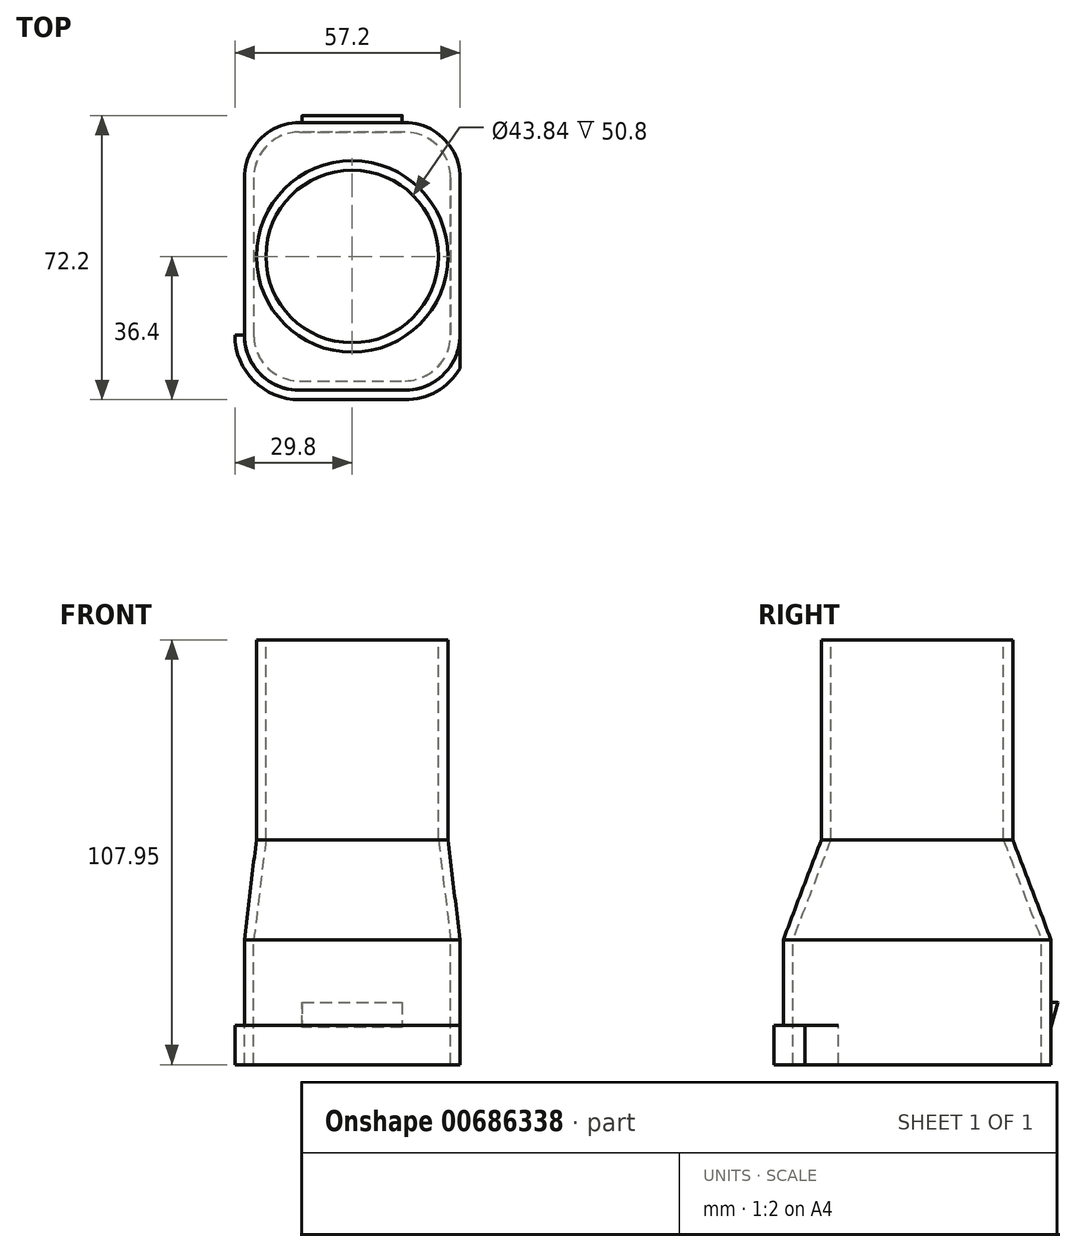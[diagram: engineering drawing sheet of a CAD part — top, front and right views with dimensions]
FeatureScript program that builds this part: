
annotation { "Feature Type Name" : "Feature", "Feature Type Description" : "" }
export const myFeature = defineFeature(function(context is Context, id is Id, definition is map)
    precondition{}
    {
        {
            var Q0;
            Q0=qCreatedBy(makeId("Top.planeOp"),FACE);
            var sketch = newSketch(context, id + "F0", { "sketchPlane" : qUnion([Q0])});
            skLineSegment(sketch, "E0.bottom", {"start": v(-13.4, 34) * mm, "end": v(13.4, 34) * mm});
            skLineSegment(sketch, "E0.top", {"start": v(-13.4, -34) * mm, "end": v(13.4, -34) * mm});
            skLineSegment(sketch, "E0.left", {"start": v(-27.4, 20) * mm, "end": v(-27.4, -20) * mm});
            skLineSegment(sketch, "E0.right", {"start": v(27.4, 20) * mm, "end": v(27.4, -20) * mm});
            skLineSegment(sketch, "E1", {"start": v(0, 0) * mm, "end": v(0, 34) * mm});
            skPoint(sketch, "E2.visualSharp", {"position": v(27.4, 34) * mm});
            skArc(sketch, "E2.filletArc", {"start": v(27.4, 20) * mm, "mid": v(23.3, 29.9) * mm, "end": v(13.4, 34) * mm});
            skPoint(sketch, "E3.visualSharp", {"position": v(27.4, -34) * mm});
            skArc(sketch, "E3.filletArc", {"start": v(13.4, -34) * mm, "mid": v(23.3, -29.9) * mm, "end": v(27.4, -20) * mm});
            skPoint(sketch, "E4.visualSharp", {"position": v(-27.4, -34) * mm});
            skArc(sketch, "E4.filletArc", {"start": v(-27.4, -20) * mm, "mid": v(-23.3, -29.9) * mm, "end": v(-13.4, -34) * mm});
            skPoint(sketch, "E5.visualSharp", {"position": v(-27.4, 34) * mm});
            skArc(sketch, "E5.filletArc", {"start": v(-13.4, 34) * mm, "mid": v(-23.3, 29.9) * mm, "end": v(-27.4, 20) * mm});
            skArc(sketch, "E6.0", {"start": v(-13.4, 31.6) * mm, "mid": v(-21.6, 28.2) * mm, "end": v(-25, 20) * mm});
            skLineSegment(sketch, "E6.1", {"start": v(-13.4, 31.6) * mm, "end": v(13.4, 31.6) * mm});
            skLineSegment(sketch, "E6.2", {"start": v(-25, 20) * mm, "end": v(-25, -20) * mm});
            skArc(sketch, "E6.3", {"start": v(25, 20) * mm, "mid": v(21.6, 28.2) * mm, "end": v(13.4, 31.6) * mm});
            skArc(sketch, "E6.4", {"start": v(-25, -20) * mm, "mid": v(-21.6, -28.2) * mm, "end": v(-13.4, -31.6) * mm});
            skLineSegment(sketch, "E6.5", {"start": v(-13.4, -31.6) * mm, "end": v(13.4, -31.6) * mm});
            skArc(sketch, "E6.6", {"start": v(13.4, -31.6) * mm, "mid": v(21.6, -28.2) * mm, "end": v(25, -20) * mm});
            skLineSegment(sketch, "E6.7", {"start": v(25, 20) * mm, "end": v(25, -20) * mm});
            skSolve(sketch);
        }
        {
            var Q0;
            Q0 = qSketchRegion(id + "F0", true);
            var Q1;
            {var subQ3=sQuery(id+"F0.wireOp",EDGE,"E6.0");Q1=makeQuery(id+"F0.imprint","IMPRINT",FACE,{"disambiguationData":[TD([[makeQuery(id+"F0.imprint","IMPRINT",EDGE,{"derivedFrom":subQ3}),1.0]])]});}
            extrude(context, id + "F1", {"entities" : qUnion([Q0, Q1]), "oppositeDirection" : true, "depth" : 31.75 * mm, "offsetDistance" : 25.4 * mm});
        }
        {
            var Q0;
            Q0=makeQuery(id+"F1.opExtrude","SWEPT_FACE",FACE,{"disambiguationData":[OSD([sQuery(id+"F0.wireOp",EDGE,"E0.bottom")])]});
            var sketch = newSketch(context, id + "F2", { "sketchPlane" : qUnion([Q0])});
            skLineSegment(sketch, "E7", {"start": v(0, 0) * mm, "end": v(0, -15.88) * mm});
            skLineSegment(sketch, "E8", {"start": v(0, -15.88) * mm, "end": v(-12.7, -15.88) * mm});
            skLineSegment(sketch, "E9.bottom", {"start": v(-12.7, -15.88) * mm, "end": v(12.7, -15.88) * mm});
            skLineSegment(sketch, "E9.top", {"start": v(-12.7, -22.22) * mm, "end": v(12.7, -22.22) * mm});
            skLineSegment(sketch, "E9.left", {"start": v(-12.7, -15.88) * mm, "end": v(-12.7, -22.22) * mm});
            skLineSegment(sketch, "E9.right", {"start": v(12.7, -15.88) * mm, "end": v(12.7, -22.22) * mm});
            skSolve(sketch);
        }
        {
            var Q0;
            Q0 = qSketchRegion(id + "F2", true);
            extrude(context, id + "F3", {"entities" : qUnion([Q0]), "operationType" : NewBodyOperationType.ADD, "depth" : 1.8 * mm, "offsetDistance" : 25.4 * mm});
        }
        {
            var Q0;
            Q0=makeQuery(id+"F3.opExtrude","SWEPT_FACE",FACE,{"disambiguationData":[OSD([sQuery(id+"F2.wireOp",EDGE,"E9.left")])]});
            var sketch = newSketch(context, id + "F4", { "sketchPlane" : qUnion([Q0])});
            skCircle(sketch, "E10", {"center": v(35.75, -15.93) * mm, "radius": 0.05 * mm});
            skLineSegment(sketch, "E11", {"start": v(35.78, -15.97) * mm, "end": v(34, -22.22) * mm});
            skLineSegment(sketch, "E12", {"start": v(34, -22.22) * mm, "end": v(35.8, -22.22) * mm});
            skLineSegment(sketch, "E13", {"start": v(35.8, -22.22) * mm, "end": v(35.8, -15.93) * mm});
            skLineSegment(sketch, "E14", {"start": v(35.8, -15.93) * mm, "end": v(35.8, -15.88) * mm});
            skLineSegment(sketch, "E15", {"start": v(35.8, -15.88) * mm, "end": v(35.75, -15.88) * mm});
            skSolve(sketch);
        }
        {
            var Q0;
            {var subQ0=sQuery(id+"F4.wireOp",EDGE,"E14");Q0=makeQuery(id+"F4.imprint","IMPRINT",FACE,{"disambiguationData":[TD([[makeQuery(id+"F4.imprint","IMPRINT",EDGE,{"derivedFrom":subQ0}),-1.0]])]});}
            var Q1;
            {var subQ0=sQuery(id+"F4.wireOp",EDGE,"E11");Q1=makeQuery(id+"F4.imprint","IMPRINT",FACE,{"disambiguationData":[TD([[makeQuery(id+"F4.imprint","IMPRINT",EDGE,{"derivedFrom":subQ0}),1.0]])]});}
            extrude(context, id + "F5", {"entities" : qUnion([Q0, Q1]), "operationType" : NewBodyOperationType.REMOVE, "endBound" : BoundingType.THROUGH_ALL, "oppositeDirection" : true, "depth" : 25.4 * mm, "offsetDistance" : 25.4 * mm});
        }
        {
            var Q0;
            Q0=qCreatedBy(makeId("Top.planeOp"),FACE);
            cPlane(context, id + "F6", {"entities" : qUnion([Q0]), "cplaneType" : CPlaneType.OFFSET, "offset" : 76.2 * mm, "width" : 152.4 * mm, "height" : 152.4 * mm});
        }
        {
            var Q0;
            Q0=qCreatedBy(id+"F6.planeOp",FACE);
            var sketch = newSketch(context, id + "F7", { "sketchPlane" : qUnion([Q0])});
            skCircle(sketch, "E16", {"center": v(0, 0) * mm, "radius": 24.32 * mm});
            skCircle(sketch, "E17", {"center": v(0, 0) * mm, "radius": 21.92 * mm});
            skSolve(sketch);
        }
        {
            var Q0;
            Q0 = qSketchRegion(id + "F7", true);
            var Q1;
            Q1=makeQuery(id+"F7.imprint","IMPRINT",FACE,{"disambiguationData":[TD([[makeQuery(id+"F7.imprint","IMPRINT",EDGE,{"derivedFrom":sQuery(id+"F7.wireOp",EDGE,"E17")}),1.0]])]});
            extrude(context, id + "F8", {"entities" : qUnion([Q0, Q1]), "oppositeDirection" : true, "depth" : 50.8 * mm, "offsetDistance" : 25.4 * mm});
        }
        {
            var Q1;
            Q1=makeQuery(id+"F1.opExtrude","CAP_FACE",FACE,{"disambiguationData":[OSD([sQuery(id+"F0.wireOp",EDGE,"E0.bottom"),sQuery(id+"F0.wireOp",EDGE,"E0.top"),sQuery(id+"F0.wireOp",EDGE,"E0.left"),sQuery(id+"F0.wireOp",EDGE,"E0.right"),sQuery(id+"F0.wireOp",EDGE,"E2.filletArc"),sQuery(id+"F0.wireOp",EDGE,"E3.filletArc"),sQuery(id+"F0.wireOp",EDGE,"E4.filletArc"),sQuery(id+"F0.wireOp",EDGE,"E5.filletArc")])],"isStart":true});
            var Q2;
            Q2=makeQuery(id+"F8.opExtrude","CAP_FACE",FACE,{"disambiguationData":[OSD([sQuery(id+"F7.wireOp",EDGE,"E16")])],"isStart":false});
            loft(context, id + "F9", {"operationType" : NewBodyOperationType.ADD, "sheetProfilesArray" : [{ "sheetProfileEntities" : qUnion([Q1]) }, { "sheetProfileEntities" : qUnion([Q2]) }]});
        }
        {
            var Q0;
            Q0=makeQuery(id+"F7.imprint","IMPRINT",FACE,{"disambiguationData":[TD([[makeQuery(id+"F7.imprint","IMPRINT",EDGE,{"derivedFrom":sQuery(id+"F7.wireOp",EDGE,"E17")}),1.0]])]});
            extrude(context, id + "F10", {"entities" : qUnion([Q0]), "operationType" : NewBodyOperationType.REMOVE, "oppositeDirection" : true, "depth" : 50.8 * mm, "offsetDistance" : 25.4 * mm});
        }
        {
            var Q0;
            {var subQ3=sQuery(id+"F0.wireOp",EDGE,"E6.0");Q0=makeQuery(id+"F0.imprint","IMPRINT",FACE,{"disambiguationData":[TD([[makeQuery(id+"F0.imprint","IMPRINT",EDGE,{"derivedFrom":subQ3}),1.0]])]});}
            extrude(context, id + "F11", {"entities" : qUnion([Q0]), "operationType" : NewBodyOperationType.REMOVE, "oppositeDirection" : true, "depth" : 50.8 * mm, "offsetDistance" : 25.4 * mm});
        }
        {
            var Q1;
            Q1=makeQuery(id+"F11.boolean.opBoolean","COPY",FACE,{"derivedFrom":makeQuery(id+"F11.opExtrude","CAP_FACE",FACE,{"disambiguationData":[OSD([sQuery(id+"F0.wireOp",EDGE,"E6.0"),sQuery(id+"F0.wireOp",EDGE,"E6.1"),sQuery(id+"F0.wireOp",EDGE,"E6.2"),sQuery(id+"F0.wireOp",EDGE,"E6.3"),sQuery(id+"F0.wireOp",EDGE,"E6.4"),sQuery(id+"F0.wireOp",EDGE,"E6.5"),sQuery(id+"F0.wireOp",EDGE,"E6.6"),sQuery(id+"F0.wireOp",EDGE,"E6.7")])],"isStart":true})});
            var Q2;
            Q2=makeQuery(id+"F10.boolean.opBoolean","COPY",FACE,{"derivedFrom":makeQuery(id+"F10.opExtrude","CAP_FACE",FACE,{"disambiguationData":[OSD([sQuery(id+"F7.wireOp",EDGE,"E17")])],"isStart":false})});
            loft(context, id + "F12", {"operationType" : NewBodyOperationType.REMOVE, "sheetProfilesArray" : [{ "sheetProfileEntities" : qUnion([Q1]) }, { "sheetProfileEntities" : qUnion([Q2]) }]});
        }
        {
            var Q0;
            Q0=makeQuery(id+"F1.opExtrude","CAP_FACE",FACE,{"disambiguationData":[OSD([sQuery(id+"F0.wireOp",EDGE,"E0.bottom"),sQuery(id+"F0.wireOp",EDGE,"E0.top"),sQuery(id+"F0.wireOp",EDGE,"E0.left"),sQuery(id+"F0.wireOp",EDGE,"E0.right"),sQuery(id+"F0.wireOp",EDGE,"E2.filletArc"),sQuery(id+"F0.wireOp",EDGE,"E3.filletArc"),sQuery(id+"F0.wireOp",EDGE,"E4.filletArc"),sQuery(id+"F0.wireOp",EDGE,"E5.filletArc")])],"isStart":false});
            var sketch = newSketch(context, id + "F13", { "sketchPlane" : qUnion([Q0])});
            skLineSegment(sketch, "E18", {"start": v(27.4, 20) * mm, "end": v(27.4, 28.54) * mm});
            skArc(sketch, "E19.0", {"start": v(13.4, 36.4) * mm, "mid": v(21.43, 34.3) * mm, "end": v(27.4, 28.54) * mm});
            skLineSegment(sketch, "E19.1", {"start": v(-13.4, 36.4) * mm, "end": v(13.4, 36.4) * mm});
            skArc(sketch, "E19.2", {"start": v(-29.8, 20) * mm, "mid": v(-25, 31.6) * mm, "end": v(-13.4, 36.4) * mm});
            skLineSegment(sketch, "E20", {"start": v(-29.8, 20) * mm, "end": v(-25, 20) * mm});
            skArc(sketch, "E21.0", {"start": v(13.4, 32) * mm, "mid": v(21.89, 28.49) * mm, "end": v(25.4, 20) * mm});
            skLineSegment(sketch, "E21.1", {"start": v(-13.4, 32) * mm, "end": v(13.4, 32) * mm});
            skArc(sketch, "E21.2", {"start": v(-25.4, 20) * mm, "mid": v(-21.89, 28.49) * mm, "end": v(-13.4, 32) * mm});
            skLineSegment(sketch, "E22", {"start": v(25.4, 20) * mm, "end": v(27.4, 20) * mm});
            skSolve(sketch);
        }
        {
            var Q0;
            Q0 = qSketchRegion(id + "F13", true);
            extrude(context, id + "F14", {"entities" : qUnion([Q0]), "operationType" : NewBodyOperationType.ADD, "oppositeDirection" : true, "depth" : 10 * mm, "offsetDistance" : 25 * mm});
        }
    });
